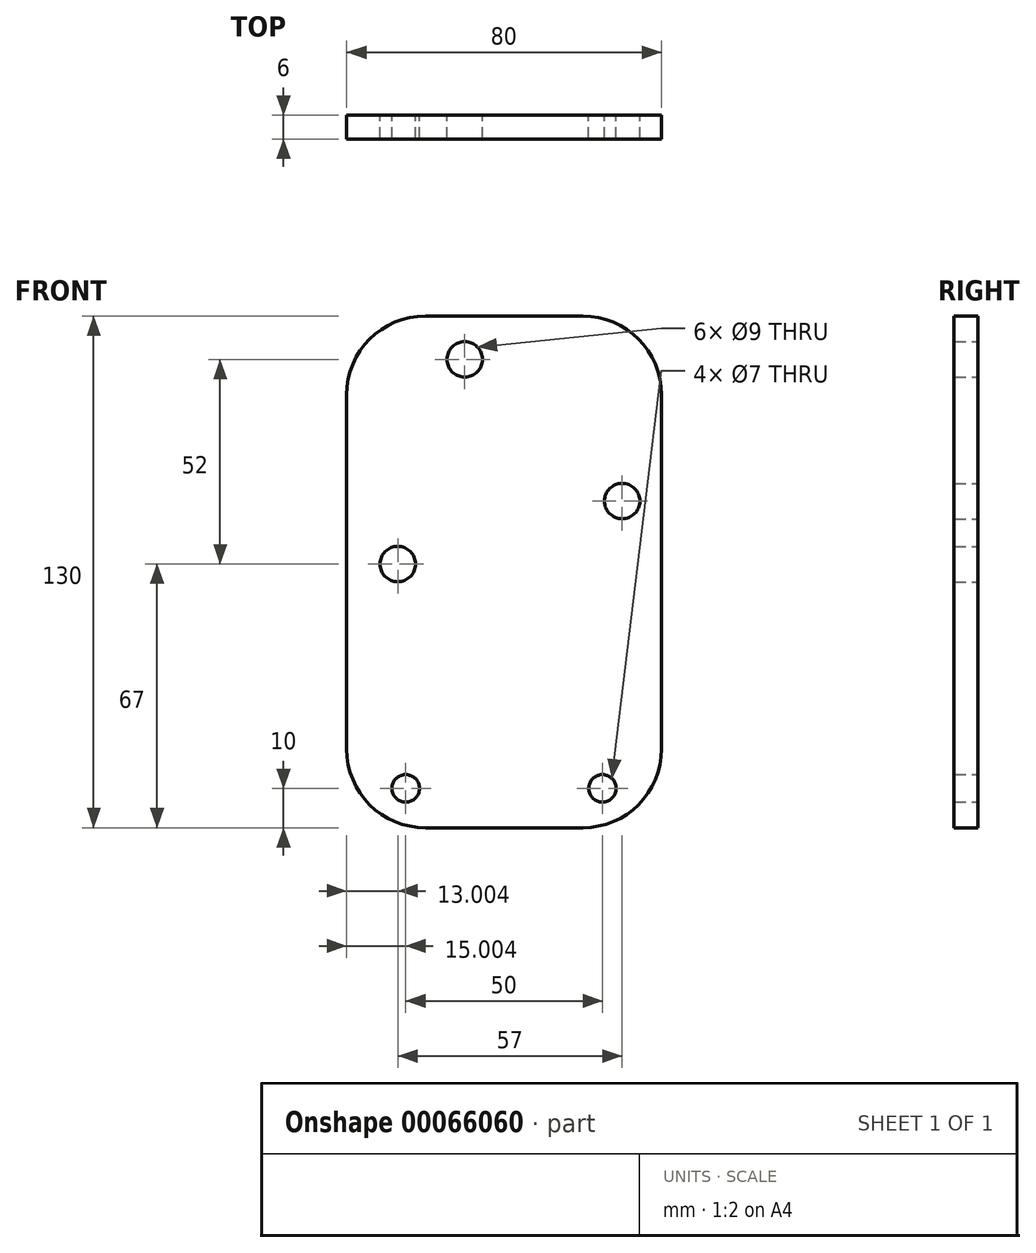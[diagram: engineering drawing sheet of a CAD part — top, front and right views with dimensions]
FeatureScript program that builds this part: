
annotation { "Feature Type Name" : "Feature", "Feature Type Description" : "" }
export const myFeature = defineFeature(function(context is Context, id is Id, definition is map)
    precondition{}
    {
        {
            var Q0;
            Q0=qCreatedBy(makeId("Front.planeOp"),FACE);
            var sketch = newSketch(context, id + "F0", { "sketchPlane" : qUnion([Q0])});
            skLineSegment(sketch, "E0.rect.bottom", {"start": v(45.36, 65) * mm, "end": v(-34.64, 65) * mm});
            skLineSegment(sketch, "E0.rect.top", {"start": v(45.36, -65) * mm, "end": v(-34.64, -65) * mm});
            skLineSegment(sketch, "E0.rect.left", {"start": v(45.36, 65) * mm, "end": v(45.36, -65) * mm});
            skLineSegment(sketch, "E0.rect.right", {"start": v(-34.64, 65) * mm, "end": v(-34.64, -65) * mm});
            skCircle(sketch, "E1", {"center": v(-4.64, 54) * mm, "radius": 4.5 * mm});
            skCircle(sketch, "E2", {"center": v(35.36, 18) * mm, "radius": 4.5 * mm});
            skCircle(sketch, "E3", {"center": v(-21.64, 2) * mm, "radius": 4.5 * mm});
            skCircle(sketch, "E4", {"center": v(30.36, -55) * mm, "radius": 3.5 * mm});
            skCircle(sketch, "E5", {"center": v(-19.64, -55) * mm, "radius": 3.5 * mm});
            skSolve(sketch);
        }
        {
            var Q0;
            Q0=makeQuery(id+"F0.imprint","IMPRINT",FACE,{"disambiguationData":[TD([[makeQuery(id+"F0.imprint","IMPRINT",EDGE,{"derivedFrom":sQuery(id+"F0.wireOp",EDGE,"E0.rect.bottom")}),1.0]])]});
            extrude(context, id + "F1", {"entities" : qUnion([Q0]), "depth" : 6 * mm});
        }
        {
            var Q0;
            Q0=makeQuery(id+"F1.opExtrude","SWEPT_EDGE",EDGE,{"disambiguationData":[OSD([sQuery(id+"F0.wireOp",EDGE,"E0.rect.bottom"),sQuery(id+"F0.wireOp",EDGE,"E0.rect.left")])]});
            var Q1;
            Q1=makeQuery(id+"F1.opExtrude","SWEPT_EDGE",EDGE,{"disambiguationData":[OSD([sQuery(id+"F0.wireOp",EDGE,"E0.rect.bottom"),sQuery(id+"F0.wireOp",EDGE,"E0.rect.right")])]});
            var Q2;
            Q2=makeQuery(id+"F1.opExtrude","SWEPT_EDGE",EDGE,{"disambiguationData":[OSD([sQuery(id+"F0.wireOp",EDGE,"E0.rect.top"),sQuery(id+"F0.wireOp",EDGE,"E0.rect.right")])]});
            var Q3;
            Q3=makeQuery(id+"F1.opExtrude","SWEPT_EDGE",EDGE,{"disambiguationData":[OSD([sQuery(id+"F0.wireOp",EDGE,"E0.rect.top"),sQuery(id+"F0.wireOp",EDGE,"E0.rect.left")])]});
            fillet(context, id + "F2", {"entities" : qUnion([Q0, Q1, Q2, Q3]), "radius" : 20 * mm, "tangentPropagation" : true, "allowEdgeOverflow" : false});
        }
    });
